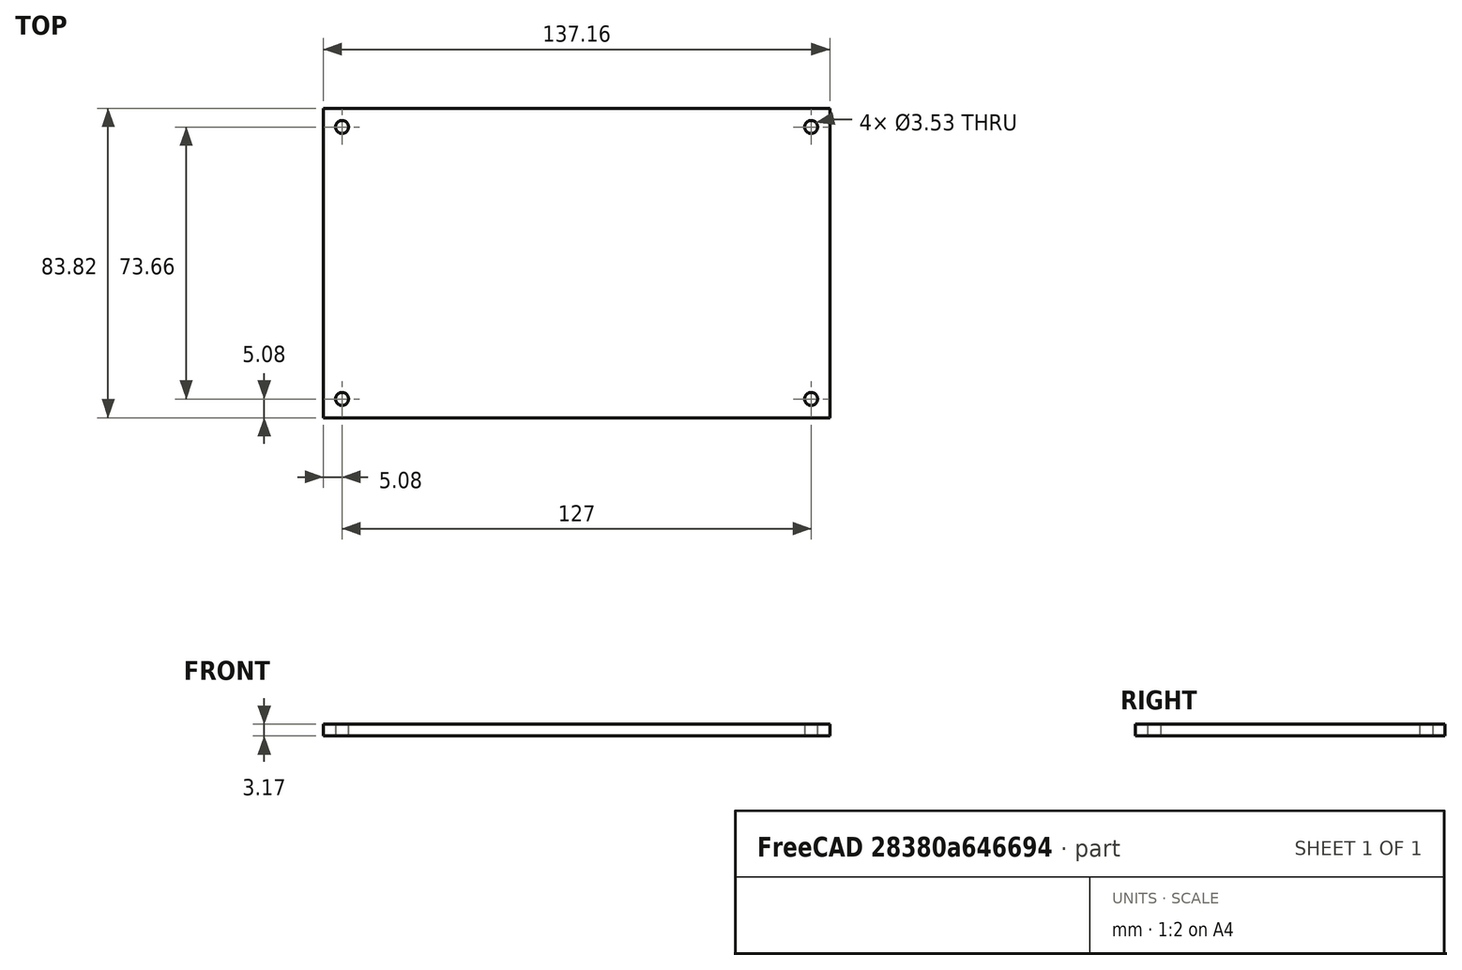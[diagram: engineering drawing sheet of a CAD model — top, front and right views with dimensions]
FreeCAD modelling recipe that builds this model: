
FCSTD DOCUMENT  (FreeCAD 1.0R39109 (Git))
Label: WorkBenchKrake
License: All rights reserved
LicenseURL: https://en.wikipedia.org/wiki/All_rights_reserved
objects: Sketcher::SketchObject×1, PartDesign::Pad×1, PartDesign::Body×1, App::Part×1
note: 6 computed .brp shape members not serialized (recipe doc carries the construction recipe); baked Part::Feature solids carry a one-line shape summary decoded from their .brp

FEATURE [Sketcher::SketchObject] Sketch
  ArcFitTolerance = 1e-06
  AttachmentSupport = -> [XY_Plane001]
  FullyConstrained = true
  MakeInternals = false
  MapMode = 5
  sketch-geometry (12):
    g0: LineSegment StartX=-68.58 StartY=41.91 StartZ=0 EndX=-68.58 EndY=-41.91 EndZ=0
    g1: LineSegment StartX=-68.58 StartY=-41.91 StartZ=0 EndX=68.58 EndY=-41.91 EndZ=0
    g2: LineSegment StartX=68.58 StartY=-41.91 StartZ=0 EndX=68.58 EndY=41.91 EndZ=0
    g3: LineSegment StartX=68.58 StartY=41.91 StartZ=0 EndX=-68.58 EndY=41.91 EndZ=0
    g4: LineSegment [constr] StartX=-63.5 StartY=36.83 StartZ=0 EndX=-63.5 EndY=-36.83 EndZ=0
    g5: LineSegment [constr] StartX=-63.5 StartY=-36.83 StartZ=0 EndX=63.5 EndY=-36.83 EndZ=0
    g6: LineSegment [constr] StartX=63.5 StartY=-36.83 StartZ=0 EndX=63.5 EndY=36.83 EndZ=0
    g7: LineSegment [constr] StartX=63.5 StartY=36.83 StartZ=0 EndX=-63.5 EndY=36.83 EndZ=0
    g8: Circle CenterX=-63.5 CenterY=-36.83 CenterZ=0 NormalX=0 NormalY=0 NormalZ=1 AngleXU=0 Radius=1.7653
    g9: Circle CenterX=-63.5 CenterY=36.83 CenterZ=0 NormalX=0 NormalY=0 NormalZ=1 AngleXU=0 Radius=1.7653
    g10: Circle CenterX=63.5 CenterY=36.83 CenterZ=0 NormalX=0 NormalY=0 NormalZ=1 AngleXU=0 Radius=1.7653
    g11: Circle CenterX=63.5 CenterY=-36.83 CenterZ=0 NormalX=0 NormalY=0 NormalZ=1 AngleXU=0 Radius=1.7653
  constraints (30):
    c: Coincident(g0,g1)
    c: Coincident(g1,g2)
    c: Coincident(g2,g3)
    c: Coincident(g3,g0)
    c: Vertical(g0)
    c: Vertical(g2)
    c: Horizontal(g1)
    c: Horizontal(g3)
    c: Symmetric(g0,g1,g-1)
    c: DistanceX(g3,g3) = 137.16
    c: DistanceY(g2,g2) = 83.82
    c: Coincident(g4,g5)
    c: Coincident(g5,g6)
    c: Coincident(g6,g7)
    c: Coincident(g7,g4)
    c: Vertical(g4)
    c: Vertical(g6)
    c: Horizontal(g5)
    c: Horizontal(g7)
    c: Symmetric(g4,g5,g-1)
    c: DistanceX(g0,g4) = 5.08
    c: DistanceY(g0,g4) = 5.08
    c: Coincident(g8,g4)
    c: Coincident(g9,g4)
    c: Coincident(g10,g6)
    c: Coincident(g11,g5)
    c: Diameter(g9) = 3.5306
    c: Equal(g9,g10)
    c: Equal(g10,g11)
    c: Equal(g11,g8)
FEATURE [PartDesign::Pad] Pad
  Direction = (0,0,1)
  Length = 3.175
  Length2 = 10
  Profile = -> Sketch
  ReferenceAxis = -> Sketch [N_Axis]
  Refine = true
  Suppressed = false
  Type = 0
FEATURE [PartDesign::Body] Body
  AllowCompound = false
  Group = -> [Sketch,Pad]
  Origin = -> Origin001
  Tip = -> Pad
FEATURE [App::Part] Part
  Group = -> [Body]
  Origin = -> Origin
